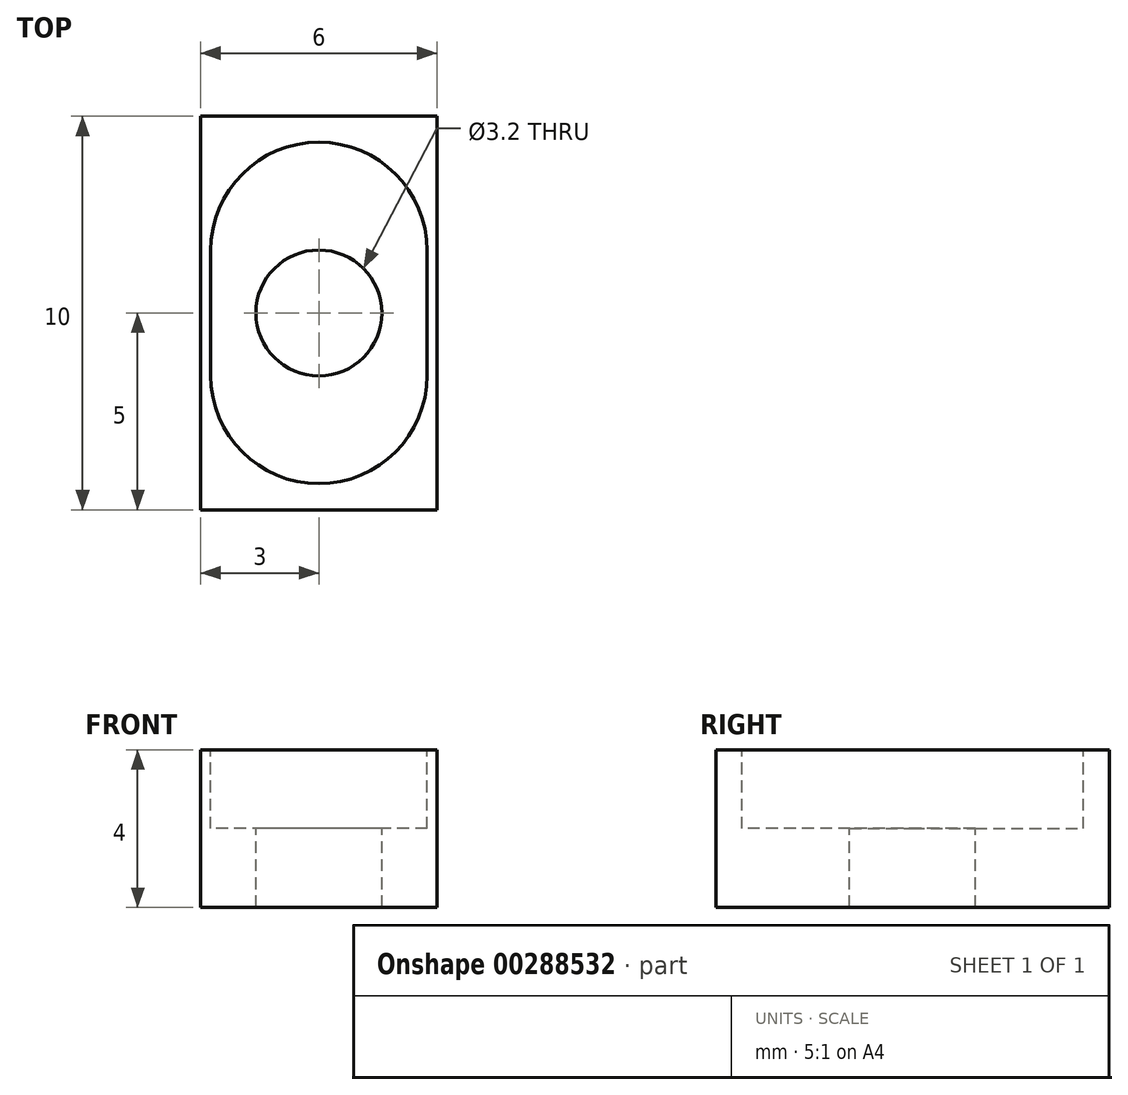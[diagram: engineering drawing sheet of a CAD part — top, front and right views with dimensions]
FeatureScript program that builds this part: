
annotation { "Feature Type Name" : "Feature", "Feature Type Description" : "" }
export const myFeature = defineFeature(function(context is Context, id is Id, definition is map)
    precondition{}
    {
        {
            var Q0;
            Q0=qCreatedBy(makeId("Top.planeOp"),FACE);
            var sketch = newSketch(context, id + "F0", { "sketchPlane" : qUnion([Q0])});
            skLineSegment(sketch, "E0.bottom", {"start": v(3, -5) * mm, "end": v(-3, -5) * mm});
            skLineSegment(sketch, "E0.top", {"start": v(3, 5) * mm, "end": v(-3, 5) * mm});
            skLineSegment(sketch, "E0.left", {"start": v(3, -5) * mm, "end": v(3, 5) * mm});
            skLineSegment(sketch, "E0.right", {"start": v(-3, -5) * mm, "end": v(-3, 5) * mm});
            skPoint(sketch, "E0.middle", {"position": v(0, 0) * mm});
            skCircle(sketch, "E1", {"center": v(0, 0) * mm, "radius": 1.6 * mm});
            skCircle(sketch, "E2.cCircle", {"center": v(0, 0) * mm, "radius": 2.75 * mm, "construction": true});
            skLineSegment(sketch, "E2.0", {"start": v(2.75, 1.59) * mm, "end": v(2.75, -1.59) * mm});
            skLineSegment(sketch, "E2.1", {"start": v(2.75, -1.59) * mm, "end": v(0, -3.18) * mm});
            skLineSegment(sketch, "E2.2", {"start": v(0, -3.18) * mm, "end": v(-2.75, -1.59) * mm});
            skLineSegment(sketch, "E2.3", {"start": v(-2.75, -1.59) * mm, "end": v(-2.75, 1.59) * mm});
            skLineSegment(sketch, "E2.4", {"start": v(-2.75, 1.59) * mm, "end": v(0, 3.18) * mm});
            skLineSegment(sketch, "E2.5", {"start": v(0, 3.18) * mm, "end": v(2.75, 1.59) * mm});
            skPoint(sketch, "E2.0.midPoint", {"position": v(2.75, 0) * mm});
            skArc(sketch, "E3", {"start": v(-2.75, -1.59) * mm, "mid": v(0, -4.34) * mm, "end": v(2.75, -1.59) * mm});
            skArc(sketch, "E4", {"start": v(-2.75, 1.59) * mm, "mid": v(0, 4.34) * mm, "end": v(2.75, 1.59) * mm});
            skSolve(sketch);
        }
        {
            var Q0;
            Q0=makeQuery(id+"F0.imprint","IMPRINT",FACE,{"disambiguationData":[TD([[makeQuery(id+"F0.imprint","IMPRINT",EDGE,{"derivedFrom":sQuery(id+"F0.wireOp",EDGE,"E0.bottom")}),-1.0]])]});
            var Q1;
            Q1=makeQuery(id+"F0.imprint","IMPRINT",FACE,{"disambiguationData":[TD([[makeQuery(id+"F0.imprint","IMPRINT",EDGE,{"derivedFrom":sQuery(id+"F0.wireOp",EDGE,"E1")}),-1.0]])]});
            var Q2;
            Q2=makeQuery(id+"F0.imprint","IMPRINT",FACE,{"disambiguationData":[TD([[makeQuery(id+"F0.imprint","IMPRINT",EDGE,{"derivedFrom":sQuery(id+"F0.wireOp",EDGE,"E2.1")}),1.0]])]});
            var Q3;
            Q3=makeQuery(id+"F0.imprint","IMPRINT",FACE,{"disambiguationData":[TD([[makeQuery(id+"F0.imprint","IMPRINT",EDGE,{"derivedFrom":sQuery(id+"F0.wireOp",EDGE,"E2.4")}),1.0]])]});
            extrude(context, id + "F1", {"entities" : qUnion([Q0, Q1, Q2, Q3]), "oppositeDirection" : true, "depth" : 4 * mm});
        }
        {
            var Q0;
            Q0=makeQuery(id+"F0.imprint","IMPRINT",FACE,{"disambiguationData":[TD([[makeQuery(id+"F0.imprint","IMPRINT",EDGE,{"derivedFrom":sQuery(id+"F0.wireOp",EDGE,"E1")}),-1.0]])]});
            var Q1;
            Q1=makeQuery(id+"F0.imprint","IMPRINT",FACE,{"disambiguationData":[TD([[makeQuery(id+"F0.imprint","IMPRINT",EDGE,{"derivedFrom":sQuery(id+"F0.wireOp",EDGE,"E2.4")}),1.0]])]});
            var Q2;
            Q2=makeQuery(id+"F0.imprint","IMPRINT",FACE,{"disambiguationData":[TD([[makeQuery(id+"F0.imprint","IMPRINT",EDGE,{"derivedFrom":sQuery(id+"F0.wireOp",EDGE,"E2.1")}),1.0]])]});
            extrude(context, id + "F2", {"entities" : qUnion([Q0, Q1, Q2]), "operationType" : NewBodyOperationType.REMOVE, "oppositeDirection" : true, "depth" : 2 * mm});
        }
    });
